# Revit family: LRTF-C29
name_source: partatom
category: Lighting Fixtures
units: mm (PartAtom-declared; Revit-internal decimal feet)

## family parameters
Cut with Voids When Loaded = No
Host = Face
Light Source = Yes
OmniClass Number = 23.80.70.11.14.17
OmniClass Title = Direct/Indirect
Part Type = Normal
Room Calculation Point = No
Round Connector Dimension = Use Diameter
Shared = No

## types (6) — shared parameters
Assembly Code = D5020200
Color Filter = 16777215
Default Elevation = 4' - 0"
Description = Wet Location Type F
Diffuser Finish = Acrylic - Viscor - Frosted Linear Ribbed
Dimming Lamp Color Temperature Shift = <None>
Emit Shape Visible in Rendering = No
Housing Finish = Metal - Viscor - White
Lamp = LED
Lens Finish = Acrylic - Viscor - Frosted Prismatic P12
Manufacturer = VISIONEERING by VISCOR
Model = LRTF-C29
Tilt Angle = -90.00°
URL = https://www.viscor.com
Voltage = 120 V

## per-type parameters (varying)
| type | Apparent Load | Emit from Rectangle Length | Emit from Rectangle Width | Lamp Wattage | Length | Photometric Web File | Reflector Width | Width |
| LRTF-C29-1X4-LED840K038LUNV | 28 VA | 3' - 11 3/4" | 0' - 11 3/4" | 28 VA | 3' - 11 3/4" | LRTF-C29-1X4-LED840K038LUNV.ies | 0' - 5 7/8" | 0' - 11 3/4" |
| LRTF-C29-2X4-LED840K040LUNV | 31 VA | 3' - 11 3/4" | 1' - 11 3/4" | 31 VA | 3' - 11 3/4" | LRTF-C29-2X4-LED840K040LUNV-G003841.IES | 0' - 11 7/8" | 1' - 11 3/4" |
| LRTF-C29-2X2-LED840K038LUNV | 34 VA | 1' - 11 3/4" | 1' - 11 3/4" | 34 VA | 1' - 11 3/4" | LRTF-C29-2X2-LED840K038LUNV-G003904.IES | 0' - 11 7/8" | 1' - 11 3/4" |
| LRTF-C29-2X4-LED840K050LUNV | 38 VA | 3' - 11 3/4" | 1' - 11 3/4" | 38 VA | 3' - 11 3/4" |  | 0' - 11 7/8" | 1' - 11 3/4" |
| LRTF-C29-1X4-LED840K050LUNV | 37 VA | 3' - 11 3/4" | 0' - 11 3/4" | 37 VA | 3' - 11 3/4" | LRTF-C29-1X4-LED840K050LUNV.ies | 0' - 5 7/8" | 0' - 11 3/4" |
| LRTF-C29-2X4-LED840K070LUNV | 55 VA | 3' - 11 3/4" | 1' - 11 3/4" | 55 VA | 3' - 11 3/4" | LRTF-C29-2X4-LED840K070LUNV-G003843.IES | 0' - 11 7/8" | 1' - 11 3/4" |

## geometry (parser evidence)
native form markers: Sweep x3
no freeform markers — native parametric forms only
